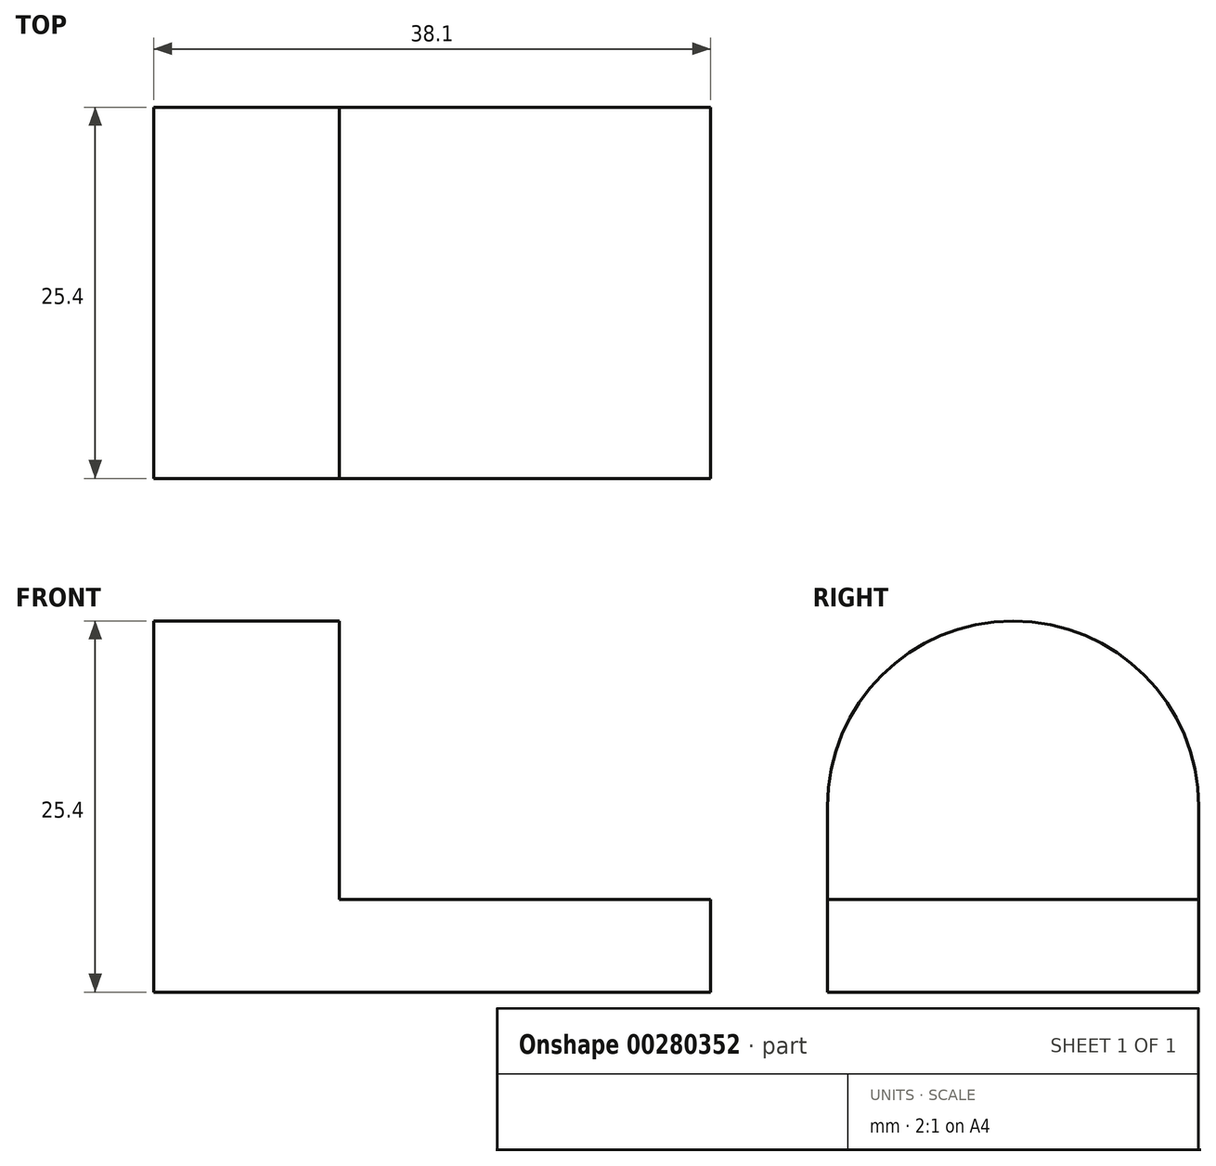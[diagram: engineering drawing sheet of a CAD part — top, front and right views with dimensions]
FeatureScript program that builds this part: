
annotation { "Feature Type Name" : "Feature", "Feature Type Description" : "" }
export const myFeature = defineFeature(function(context is Context, id is Id, definition is map)
    precondition{}
    {
        {
            var Q0;
            Q0=qCreatedBy(makeId("Top.planeOp"),FACE);
            var sketch = newSketch(context, id + "F0", { "sketchPlane" : qUnion([Q0])});
            skLineSegment(sketch, "E0.bottom", {"start": v(0, 0) * mm, "end": v(38.1, 0) * mm});
            skLineSegment(sketch, "E0.top", {"start": v(0, 25.4) * mm, "end": v(38.1, 25.4) * mm});
            skLineSegment(sketch, "E0.left", {"start": v(0, 0) * mm, "end": v(0, 25.4) * mm});
            skLineSegment(sketch, "E0.right", {"start": v(38.1, 0) * mm, "end": v(38.1, 25.4) * mm});
            skSolve(sketch);
        }
        {
            var Q0;
            Q0 = qSketchRegion(id + "F0", true);
            extrude(context, id + "F1", {"entities" : qUnion([Q0]), "depth" : 25.4 * mm});
        }
        {
            var Q0;
            Q0=makeQuery(id+"F1.opExtrude","CAP_FACE",FACE,{"disambiguationData":[OSD([sQuery(id+"F0.wireOp",EDGE,"E0.bottom"),sQuery(id+"F0.wireOp",EDGE,"E0.top"),sQuery(id+"F0.wireOp",EDGE,"E0.left"),sQuery(id+"F0.wireOp",EDGE,"E0.right")])],"isStart":false});
            var sketch = newSketch(context, id + "F2", { "sketchPlane" : qUnion([Q0])});
            skLineSegment(sketch, "E1.bottom", {"start": v(38.1, 0) * mm, "end": v(12.7, 0) * mm});
            skLineSegment(sketch, "E1.top", {"start": v(38.1, 25.4) * mm, "end": v(12.7, 25.4) * mm});
            skLineSegment(sketch, "E1.left", {"start": v(38.1, 0) * mm, "end": v(38.1, 25.4) * mm});
            skLineSegment(sketch, "E1.right", {"start": v(12.7, 0) * mm, "end": v(12.7, 25.4) * mm});
            skSolve(sketch);
        }
        {
            var Q0;
            Q0 = qSketchRegion(id + "F2", true);
            extrude(context, id + "F3", {"entities" : qUnion([Q0]), "operationType" : NewBodyOperationType.REMOVE, "oppositeDirection" : true, "depth" : 19.05 * mm});
        }
        {
            var Q0;
            Q0=makeQuery(id+"F3.boolean.opBoolean","COPY",FACE,{"derivedFrom":makeQuery(id+"F3.opExtrude","SWEPT_FACE",FACE,{"disambiguationData":[OSD([sQuery(id+"F2.wireOp",EDGE,"E1.right")])]})});
            var sketch = newSketch(context, id + "F4", { "sketchPlane" : qUnion([Q0])});
            skArc(sketch, "E2", {"start": v(25.4, 12.7) * mm, "mid": v(12.7, 25.4) * mm, "end": v(0, 12.7) * mm});
            skLineSegment(sketch, "E3", {"start": v(0, 12.7) * mm, "end": v(0, 25.4) * mm});
            skLineSegment(sketch, "E4", {"start": v(0, 25.4) * mm, "end": v(12.7, 25.4) * mm});
            skLineSegment(sketch, "E5", {"start": v(12.7, 25.4) * mm, "end": v(25.4, 25.4) * mm});
            skLineSegment(sketch, "E6", {"start": v(25.4, 25.4) * mm, "end": v(25.4, 12.7) * mm});
            skSolve(sketch);
        }
        {
            var Q0;
            Q0 = qSketchRegion(id + "F4", true);
            extrude(context, id + "F5", {"entities" : qUnion([Q0]), "operationType" : NewBodyOperationType.REMOVE, "oppositeDirection" : true, "depth" : 25.4 * mm});
        }
    });
